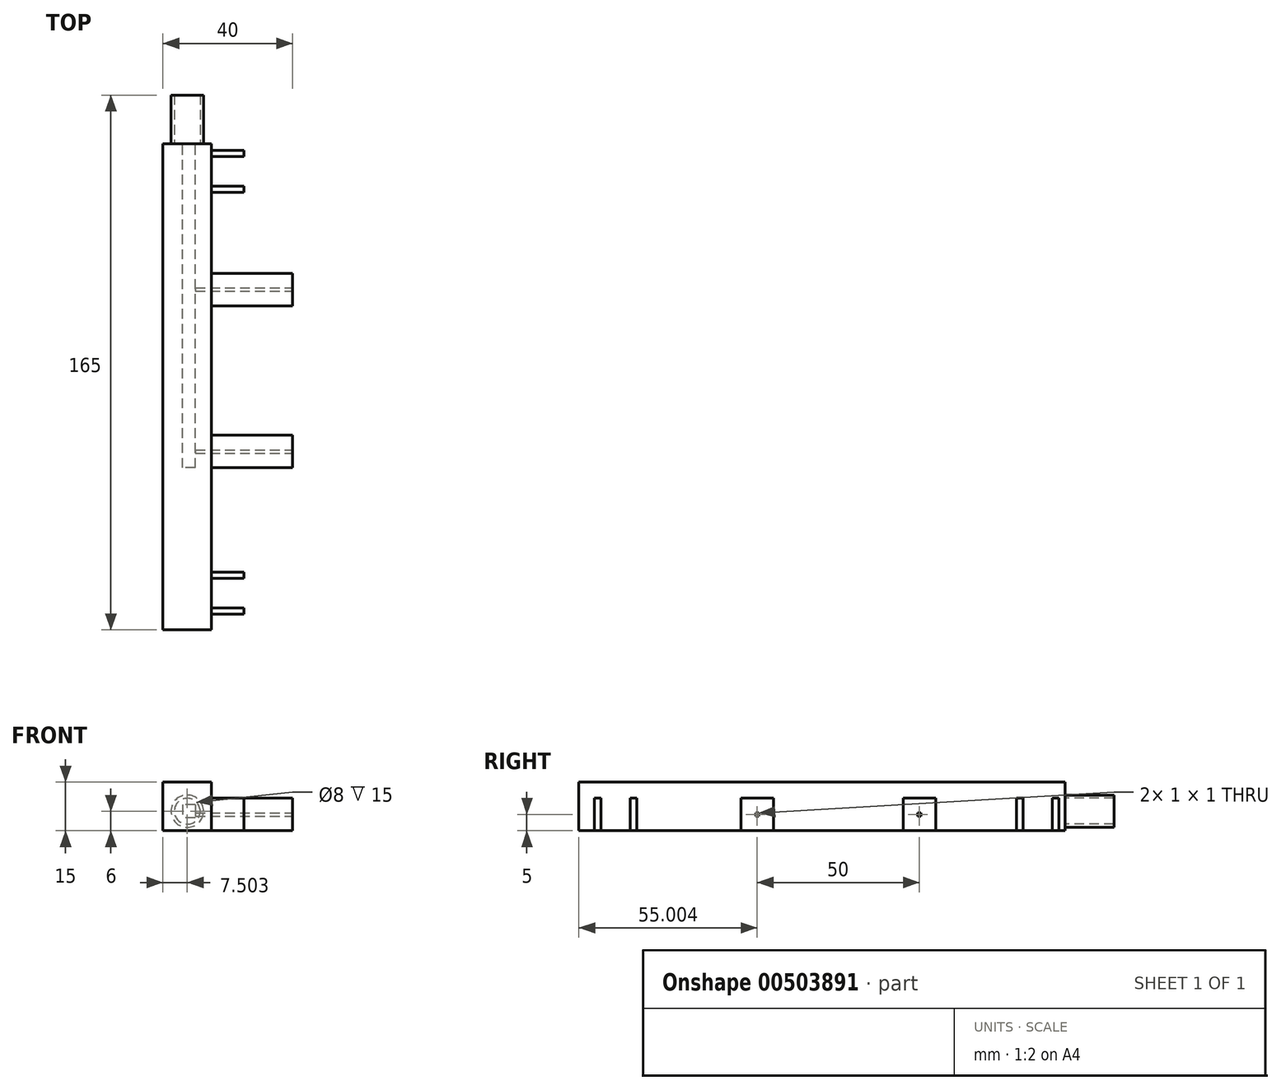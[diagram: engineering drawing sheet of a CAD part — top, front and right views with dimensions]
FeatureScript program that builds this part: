
annotation { "Feature Type Name" : "Feature", "Feature Type Description" : "" }
export const myFeature = defineFeature(function(context is Context, id is Id, definition is map)
    precondition{}
    {
        {
            var Q0;
            Q0=qCreatedBy(makeId("Top.planeOp"),FACE);
            var sketch = newSketch(context, id + "F0", { "sketchPlane" : qUnion([Q0])});
            skLineSegment(sketch, "E0.bottom", {"start": v(-44.8, 70.37) * mm, "end": v(-29.8, 70.37) * mm});
            skLineSegment(sketch, "E0.top", {"start": v(-44.8, -79.63) * mm, "end": v(-29.8, -79.63) * mm});
            skLineSegment(sketch, "E0.left", {"start": v(-44.8, 70.37) * mm, "end": v(-44.8, -79.63) * mm});
            skLineSegment(sketch, "E0.right", {"start": v(-29.8, 70.37) * mm, "end": v(-29.8, -79.63) * mm});
            skLineSegment(sketch, "E1.bottom", {"start": v(-29.8, 30.37) * mm, "end": v(-4.8, 30.37) * mm});
            skLineSegment(sketch, "E1.top", {"start": v(-29.8, 20.37) * mm, "end": v(-4.8, 20.37) * mm});
            skLineSegment(sketch, "E1.left", {"start": v(-29.8, 30.37) * mm, "end": v(-29.8, 20.37) * mm});
            skLineSegment(sketch, "E1.right", {"start": v(-4.8, 30.37) * mm, "end": v(-4.8, 20.37) * mm});
            skLineSegment(sketch, "E2.bottom", {"start": v(-29.8, -19.63) * mm, "end": v(-4.8, -19.63) * mm});
            skLineSegment(sketch, "E2.top", {"start": v(-29.8, -29.63) * mm, "end": v(-4.8, -29.63) * mm});
            skLineSegment(sketch, "E2.left", {"start": v(-29.8, -19.63) * mm, "end": v(-29.8, -29.63) * mm});
            skLineSegment(sketch, "E2.right", {"start": v(-4.8, -19.63) * mm, "end": v(-4.8, -29.63) * mm});
            skLineSegment(sketch, "E3.bottom", {"start": v(-29.8, -61.82) * mm, "end": v(-19.8, -61.82) * mm});
            skLineSegment(sketch, "E3.top", {"start": v(-29.8, -63.82) * mm, "end": v(-19.8, -63.82) * mm});
            skLineSegment(sketch, "E3.left", {"start": v(-29.8, -61.82) * mm, "end": v(-29.8, -63.82) * mm});
            skLineSegment(sketch, "E3.right", {"start": v(-19.8, -61.82) * mm, "end": v(-19.8, -63.82) * mm});
            skLineSegment(sketch, "E4.bottom", {"start": v(-22.3, -63.82) * mm, "end": v(-19.8, -63.82) * mm});
            skLineSegment(sketch, "E4.top", {"start": v(-22.3, -72.87) * mm, "end": v(-19.8, -72.87) * mm});
            skLineSegment(sketch, "E4.left", {"start": v(-22.3, -63.82) * mm, "end": v(-22.3, -72.87) * mm});
            skLineSegment(sketch, "E4.right", {"start": v(-19.8, -63.82) * mm, "end": v(-19.8, -72.87) * mm});
            skLineSegment(sketch, "E5.bottom", {"start": v(-29.8, -72.87) * mm, "end": v(-19.8, -72.87) * mm});
            skLineSegment(sketch, "E5.top", {"start": v(-29.8, -74.87) * mm, "end": v(-19.8, -74.87) * mm});
            skLineSegment(sketch, "E5.left", {"start": v(-29.8, -72.87) * mm, "end": v(-29.8, -74.87) * mm});
            skLineSegment(sketch, "E5.right", {"start": v(-19.8, -72.87) * mm, "end": v(-19.8, -74.87) * mm});
            skLineSegment(sketch, "E6.bottom", {"start": v(-29.8, 68.36) * mm, "end": v(-19.8, 68.36) * mm});
            skLineSegment(sketch, "E6.top", {"start": v(-29.8, 66.36) * mm, "end": v(-19.8, 66.36) * mm});
            skLineSegment(sketch, "E6.left", {"start": v(-29.8, 68.36) * mm, "end": v(-29.8, 66.36) * mm});
            skLineSegment(sketch, "E6.right", {"start": v(-19.8, 68.36) * mm, "end": v(-19.8, 66.36) * mm});
            skLineSegment(sketch, "E7.bottom", {"start": v(-22.3, 66.36) * mm, "end": v(-19.8, 66.36) * mm});
            skLineSegment(sketch, "E7.top", {"start": v(-22.3, 57.31) * mm, "end": v(-19.8, 57.31) * mm});
            skLineSegment(sketch, "E7.left", {"start": v(-22.3, 66.36) * mm, "end": v(-22.3, 57.31) * mm});
            skLineSegment(sketch, "E7.right", {"start": v(-19.8, 66.36) * mm, "end": v(-19.8, 57.31) * mm});
            skLineSegment(sketch, "E8.bottom", {"start": v(-29.8, 57.31) * mm, "end": v(-19.8, 57.31) * mm});
            skLineSegment(sketch, "E8.top", {"start": v(-29.8, 55.31) * mm, "end": v(-19.8, 55.31) * mm});
            skLineSegment(sketch, "E8.left", {"start": v(-29.8, 57.31) * mm, "end": v(-29.8, 55.31) * mm});
            skLineSegment(sketch, "E8.right", {"start": v(-19.8, 57.31) * mm, "end": v(-19.8, 55.31) * mm});
            skSolve(sketch);
        }
        {
            var Q0;
            Q0=makeQuery(id+"F0.imprint","IMPRINT",FACE,{"disambiguationData":[TD([[makeQuery(id+"F0.imprint","IMPRINT",EDGE,{"derivedFrom":sQuery(id+"F0.wireOp",EDGE,"E0.bottom")}),-1.0]])]});
            extrude(context, id + "F1", {"entities" : qUnion([Q0]), "depth" : 15 * mm});
        }
        {
            var Q0;
            Q0=makeQuery(id+"F0.imprint","IMPRINT",FACE,{"disambiguationData":[TD([[makeQuery(id+"F0.imprint","IMPRINT",EDGE,{"derivedFrom":sQuery(id+"F0.wireOp",EDGE,"E1.bottom")}),-1.0]])]});
            var Q1;
            Q1=makeQuery(id+"F0.imprint","IMPRINT",FACE,{"disambiguationData":[TD([[makeQuery(id+"F0.imprint","IMPRINT",EDGE,{"derivedFrom":sQuery(id+"F0.wireOp",EDGE,"E2.bottom")}),-1.0]])]});
            var Q2;
            Q2=makeQuery(id+"F0.imprint","IMPRINT",FACE,{"disambiguationData":[TD([[makeQuery(id+"F0.imprint","IMPRINT",EDGE,{"derivedFrom":sQuery(id+"F0.wireOp",EDGE,"E3.bottom")}),-1.0]])]});
            var Q3;
            Q3=makeQuery(id+"F0.imprint","IMPRINT",FACE,{"disambiguationData":[TD([[makeQuery(id+"F0.imprint","IMPRINT",EDGE,{"derivedFrom":sQuery(id+"F0.wireOp",EDGE,"E4.bottom")}),-1.0]])]});
            var Q4;
            Q4=makeQuery(id+"F0.imprint","IMPRINT",FACE,{"disambiguationData":[TD([[makeQuery(id+"F0.imprint","IMPRINT",EDGE,{"derivedFrom":sQuery(id+"F0.wireOp",EDGE,"E5.top")}),1.0]])]});
            var Q5;
            Q5=makeQuery(id+"F0.imprint","IMPRINT",FACE,{"disambiguationData":[TD([[makeQuery(id+"F0.imprint","IMPRINT",EDGE,{"derivedFrom":sQuery(id+"F0.wireOp",EDGE,"E8.top")}),1.0]])]});
            var Q6;
            Q6=makeQuery(id+"F0.imprint","IMPRINT",FACE,{"disambiguationData":[TD([[makeQuery(id+"F0.imprint","IMPRINT",EDGE,{"derivedFrom":sQuery(id+"F0.wireOp",EDGE,"E7.bottom")}),-1.0]])]});
            var Q7;
            Q7=makeQuery(id+"F0.imprint","IMPRINT",FACE,{"disambiguationData":[TD([[makeQuery(id+"F0.imprint","IMPRINT",EDGE,{"derivedFrom":sQuery(id+"F0.wireOp",EDGE,"E6.bottom")}),-1.0]])]});
            var Q8;
            Q8=sQuery(id+"F0.wireOp",EDGE,"E3.top");
            var Q9;
            Q9=sQuery(id+"F0.wireOp",EDGE,"E3.bottom");
            var Q10;
            Q10=sQuery(id+"F0.wireOp",EDGE,"E4.right");
            var Q11;
            Q11=sQuery(id+"F0.wireOp",EDGE,"E4.left");
            var Q12;
            Q12=sQuery(id+"F0.wireOp",EDGE,"E5.bottom");
            var Q13;
            Q13=sQuery(id+"F0.wireOp",EDGE,"E5.top");
            var Q14;
            Q14=sQuery(id+"F0.wireOp",EDGE,"E3.right");
            var Q15;
            Q15=sQuery(id+"F0.wireOp",EDGE,"E5.right");
            var Q16;
            Q16=sQuery(id+"F0.wireOp",EDGE,"E2.bottom");
            var Q17;
            Q17=sQuery(id+"F0.wireOp",EDGE,"E2.right");
            var Q18;
            Q18=sQuery(id+"F0.wireOp",EDGE,"E2.top");
            var Q19;
            Q19=sQuery(id+"F0.wireOp",EDGE,"E2.left");
            extrude(context, id + "F2", {"entities" : qUnion([Q0, Q1, Q2, Q3, Q4, Q5, Q6, Q7]), "operationType" : NewBodyOperationType.ADD, "surfaceEntities" : qUnion([Q8, Q9, Q10, Q11, Q12, Q13, Q14, Q15, Q16, Q17, Q18, Q19]), "depth" : 10 * mm});
        }
        {
            var Q0;
            Q0=makeQuery(id+"F1.opExtrude","SWEPT_FACE",FACE,{"disambiguationData":[OSD([sQuery(id+"F0.wireOp",EDGE,"E0.bottom")])]});
            var sketch = newSketch(context, id + "F3", { "sketchPlane" : qUnion([Q0])});
            skLineSegment(sketch, "E9.bottom", {"start": v(34.8, 8) * mm, "end": v(38.8, 8) * mm});
            skLineSegment(sketch, "E9.top", {"start": v(34.8, 4) * mm, "end": v(38.8, 4) * mm});
            skLineSegment(sketch, "E9.left", {"start": v(34.8, 8) * mm, "end": v(34.8, 4) * mm});
            skLineSegment(sketch, "E9.right", {"start": v(38.8, 8) * mm, "end": v(38.8, 4) * mm});
            skSolve(sketch);
        }
        {
            var Q0;
            Q0=makeQuery(id+"F3.imprint","IMPRINT",FACE,{"disambiguationData":[TD([[makeQuery(id+"F3.imprint","IMPRINT",EDGE,{"derivedFrom":sQuery(id+"F3.wireOp",EDGE,"E9.bottom")}),-1.0]])]});
            extrude(context, id + "F4", {"entities" : qUnion([Q0]), "operationType" : NewBodyOperationType.REMOVE, "oppositeDirection" : true, "depth" : 100 * mm});
        }
        {
            var Q0;
            Q0=makeQuery(id+"F2.opExtrude","SWEPT_FACE",FACE,{"disambiguationData":[OSD([sQuery(id+"F0.wireOp",EDGE,"E2.right")])]});
            var sketch = newSketch(context, id + "F5", { "sketchPlane" : qUnion([Q0])});
            skLineSegment(sketch, "E10.bottom", {"start": v(-24.13, 5.5) * mm, "end": v(-25.13, 5.5) * mm});
            skLineSegment(sketch, "E10.top", {"start": v(-24.13, 4.5) * mm, "end": v(-25.13, 4.5) * mm});
            skLineSegment(sketch, "E10.left", {"start": v(-24.13, 5.5) * mm, "end": v(-24.13, 4.5) * mm});
            skLineSegment(sketch, "E10.right", {"start": v(-25.13, 5.5) * mm, "end": v(-25.13, 4.5) * mm});
            skSolve(sketch);
        }
        {
            var Q0;
            Q0=makeQuery(id+"F2.opExtrude","SWEPT_FACE",FACE,{"disambiguationData":[OSD([sQuery(id+"F0.wireOp",EDGE,"E1.right")])]});
            var sketch = newSketch(context, id + "F6", { "sketchPlane" : qUnion([Q0])});
            skLineSegment(sketch, "E11.bottom", {"start": v(25.87, 5.5) * mm, "end": v(24.87, 5.5) * mm});
            skLineSegment(sketch, "E11.top", {"start": v(25.87, 4.5) * mm, "end": v(24.87, 4.5) * mm});
            skLineSegment(sketch, "E11.left", {"start": v(25.87, 5.5) * mm, "end": v(25.87, 4.5) * mm});
            skLineSegment(sketch, "E11.right", {"start": v(24.87, 5.5) * mm, "end": v(24.87, 4.5) * mm});
            skSolve(sketch);
        }
        {
            var Q0;
            Q0=makeQuery(id+"F6.imprint","IMPRINT",FACE,{"disambiguationData":[TD([[makeQuery(id+"F6.imprint","IMPRINT",EDGE,{"derivedFrom":sQuery(id+"F6.wireOp",EDGE,"E11.bottom")}),1.0]])]});
            var Q1;
            Q1=makeQuery(id+"F5.imprint","IMPRINT",FACE,{"disambiguationData":[TD([[makeQuery(id+"F5.imprint","IMPRINT",EDGE,{"derivedFrom":sQuery(id+"F5.wireOp",EDGE,"E10.bottom")}),1.0]])]});
            extrude(context, id + "F7", {"entities" : qUnion([Q0, Q1]), "operationType" : NewBodyOperationType.REMOVE, "oppositeDirection" : true, "depth" : 30 * mm});
        }
        {
            var Q0;
            Q0=makeQuery(id+"F1.opExtrude","SWEPT_FACE",FACE,{"disambiguationData":[OSD([sQuery(id+"F0.wireOp",EDGE,"E0.bottom")])]});
            var sketch = newSketch(context, id + "F8", { "sketchPlane" : qUnion([Q0])});
            skCircle(sketch, "E12", {"center": v(37.3, 6) * mm, "radius": 4 * mm});
            skCircle(sketch, "E13", {"center": v(37.3, 6) * mm, "radius": 5 * mm});
            skSolve(sketch);
        }
        {
            var Q0;
            {var subQ1=makeQuery(id+"F4.boolean.opBoolean","COPY",EDGE,{"derivedFrom":makeQuery(id+"F4.opExtrude","CAP_EDGE",EDGE,{"disambiguationData":[OSD([sQuery(id+"F3.wireOp",EDGE,"E9.bottom")])],"isStart":true})});var subQ3=sQuery(id+"F8.wireOp",EDGE,"E12");var subQ4=makeQuery(id+"F8.imprint","INTERSECT",VERTEX,{"derivedFrom":[subQ1,subQ3]});Q0=makeQuery(id+"F8.imprint","IMPRINT",FACE,{"disambiguationData":[TD([[makeQuery(id+"F8.imprint","IMPRINT",EDGE,{"disambiguationData":[TD([[subQ4,1.0]])],"derivedFrom":subQ3}),-1.0]])]});}
            extrude(context, id + "F9", {"entities" : qUnion([Q0]), "operationType" : NewBodyOperationType.ADD, "depth" : 15 * mm});
        }
    });
